# Revit family: O14601001_Lavamanos Vessel Razionale
name_source: partatom
category: Plumbing Fixtures
units: mm (PartAtom-declared; Revit-internal decimal feet)

## family parameters
Always vertical = Yes
Cut with Voids When Loaded = No
Host = Wall
OmniClass Number = 23.31.13.11
OmniClass Title = Single Sinks
Part Type = Normal
Room Calculation Point = No
Round Connector Dimension = Use Diameter
Shared = No

## types (1)
- Type 1
    Colección = Minimal
    Creado por = BIMBAU
    Default Elevation = 0 mm  [stored 0 ft]
    Depth = 470 mm  [stored 1.54199 ft]
    Description = Lavamanos Vessel cuadrado con agujero de rebose integral con tapón cromado. Único lavamanos vessel con agujeros insinuados que permiten escoger diferentes opciones de grifería
    Diameter = 13 mm
    Diameter 2 = 51 mm
    Fecha de creación = 08/04/2021
    Garantia = GarantiaCorona limitada de por vida
    Incluye = Desagüe sifón push cromado
    Manufacturer = Corona
    Material = Corona_Porcelana_Sanitaria
    Model = Razionale
    Peso = 17.7kg
    Productos Compatibles = Grifería monocontrol media
    Profundidad de Pozo = 11.5 cm
    Referencia = O14601001
    Resistencia = Alta resistencia al rayado y cambios de temperatura
    SKU = O14601001
    Tipo de desague = Expuesto
    Tipo de instalación = A pared
    URL = https://corona.co
    Uso = Residencial
    Width = 465 mm  [stored 1.52559 ft]

note: [stored X ft] marks values corroborated as IEEE doubles in the binary element streams (Revit-internal decimal feet)

## geometry (parser evidence)
native form markers: Sweep x7
no freeform markers — native parametric forms only
